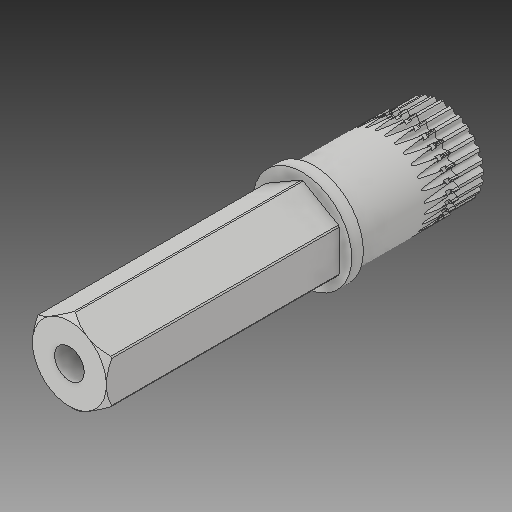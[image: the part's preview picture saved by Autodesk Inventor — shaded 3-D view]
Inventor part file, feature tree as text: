
AUTODESK INVENTOR PART (.ipt)
format: ipt  version: 2017 (Build 210142000, 142)  size: 1,415,680 bytes
history: native  units: in
note: dims shown in document units (in); Inventor stores cm internally (conversion verified against a paired STEP export)
features: fillet x1
ambient origin geometry x8: Origin, YZ Plane, XZ Plane, XY Plane, X Axis, Y Axis, Z Axis, Center Point
bodies: Solid1 (feature_tree)
feature tree (1):
  fillet  "Fillet5"  [1 undecoded]
note: 1 required parameter value undecoded (feature->parameter linkage not recoverable at this tier; creation-order binding heuristic only, values carry confidence <= 0.55)
